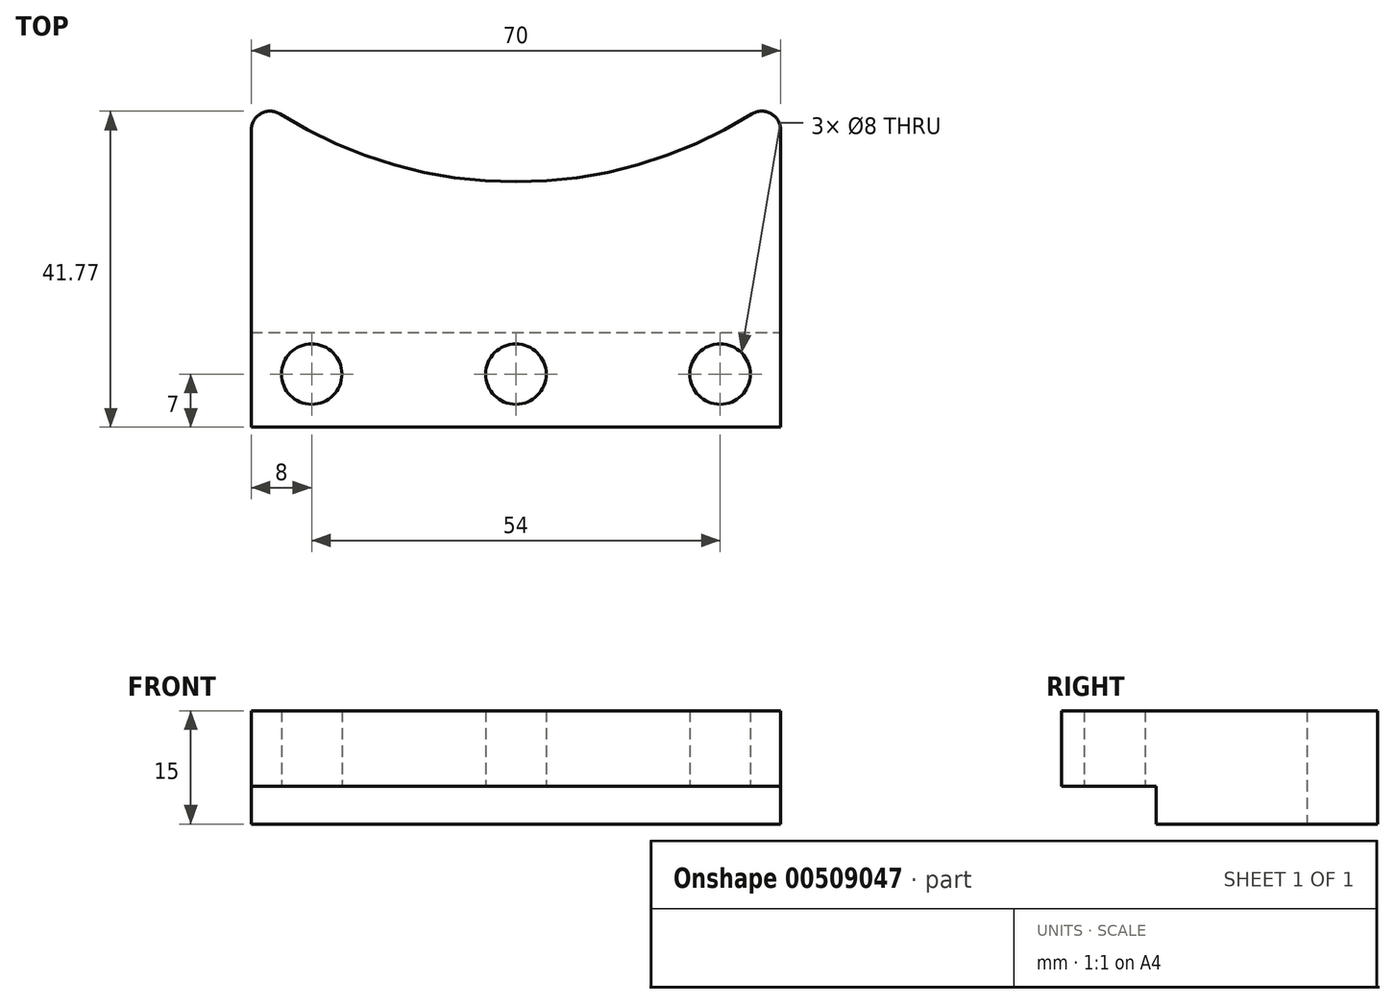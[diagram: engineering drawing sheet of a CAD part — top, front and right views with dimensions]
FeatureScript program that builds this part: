
annotation { "Feature Type Name" : "Feature", "Feature Type Description" : "" }
export const myFeature = defineFeature(function(context is Context, id is Id, definition is map)
    precondition{}
    {
        {
            var Q0;
            Q0=qCreatedBy(makeId("Top.planeOp"),FACE);
            var sketch = newSketch(context, id + "F0", { "sketchPlane" : qUnion([Q0])});
            skLineSegment(sketch, "E0.bottom", {"start": v(-35, 22) * mm, "end": v(35, 22) * mm, "construction": true});
            skLineSegment(sketch, "E0.top", {"start": v(-35, -22) * mm, "end": v(35, -22) * mm});
            skLineSegment(sketch, "E0.left", {"start": v(-35, 22) * mm, "end": v(-35, -22) * mm});
            skLineSegment(sketch, "E0.right", {"start": v(35, 22) * mm, "end": v(35, -22) * mm});
            skPoint(sketch, "E0.middle", {"position": v(0, 0) * mm});
            skLineSegment(sketch, "E1", {"start": v(0, -22) * mm, "end": v(0, 10.43) * mm, "construction": true});
            skArc(sketch, "E2", {"start": v(-35, 22) * mm, "mid": v(0, 10.43) * mm, "end": v(35, 22) * mm});
            skLineSegment(sketch, "E3", {"start": v(-35, -22) * mm, "end": v(-35, -15) * mm, "construction": true});
            skLineSegment(sketch, "E4", {"start": v(35, -15) * mm, "end": v(-35, -15) * mm, "construction": true});
            skCircle(sketch, "E5", {"center": v(0, -15) * mm, "radius": 4 * mm});
            skLineSegment(sketch, "E6", {"start": v(0, -15) * mm, "end": v(-27, -15) * mm, "construction": true});
            skLineSegment(sketch, "E7", {"start": v(0, -15) * mm, "end": v(27, -15) * mm, "construction": true});
            skCircle(sketch, "E8", {"center": v(-27, -15) * mm, "radius": 4 * mm});
            skCircle(sketch, "E9", {"center": v(27, -15) * mm, "radius": 4 * mm});
            skSolve(sketch);
        }
        {
            var Q0;
            Q0=makeQuery(id+"F0.imprint","IMPRINT",FACE,{"disambiguationData":[TD([[makeQuery(id+"F0.imprint","IMPRINT",EDGE,{"derivedFrom":sQuery(id+"F0.wireOp",EDGE,"E0.top")}),1.0]])]});
            extrude(context, id + "F1", {"entities" : qUnion([Q0]), "depth" : 40 * mm});
        }
        {
            var Q0;
            Q0=makeQuery(id+"F1.opExtrude","SWEPT_FACE",FACE,{"disambiguationData":[OSD([sQuery(id+"F0.wireOp",EDGE,"E0.right")])]});
            var sketch = newSketch(context, id + "F2", { "sketchPlane" : qUnion([Q0])});
            skLineSegment(sketch, "E10", {"start": v(-22, 0) * mm, "end": v(-9.5, 0) * mm, "construction": true});
            skLineSegment(sketch, "E11", {"start": v(-9.5, 0) * mm, "end": v(-9.5, 30) * mm});
            skLineSegment(sketch, "E12", {"start": v(-9.5, 30) * mm, "end": v(-22, 30) * mm});
            skSolve(sketch);
        }
        {
            var Q0;
            {var subQ0=sQuery(id+"F2.wireOp",EDGE,"E11");Q0=makeQuery(id+"F2.imprint","IMPRINT",FACE,{"disambiguationData":[TD([[makeQuery(id+"F2.imprint","IMPRINT",EDGE,{"derivedFrom":subQ0}),1.0]])]});}
            extrude(context, id + "F3", {"entities" : qUnion([Q0]), "operationType" : NewBodyOperationType.REMOVE, "oppositeDirection" : true, "depth" : 70 * mm});
        }
        {
            var Q0;
            Q0=makeQuery(id+"F1.opExtrude","SWEPT_EDGE",EDGE,{"disambiguationData":[OSD([sQuery(id+"F0.wireOp",EDGE,"E0.right"),sQuery(id+"F0.wireOp",EDGE,"E2")])]});
            var Q1;
            Q1=makeQuery(id+"F1.opExtrude","SWEPT_EDGE",EDGE,{"disambiguationData":[OSD([sQuery(id+"F0.wireOp",EDGE,"E0.left"),sQuery(id+"F0.wireOp",EDGE,"E2")])]});
            fillet(context, id + "F4", {"entities" : qUnion([Q0, Q1]), "radius" : 2.5 * mm, "tangentPropagation" : true, "allowEdgeOverflow" : false});
        }
        {
            var Q0;
            Q0=makeQuery(id+"F1.opExtrude","CAP_FACE",FACE,{"disambiguationData":[OSD([sQuery(id+"F0.wireOp",EDGE,"E0.top"),sQuery(id+"F0.wireOp",EDGE,"E0.left"),sQuery(id+"F0.wireOp",EDGE,"E0.right"),sQuery(id+"F0.wireOp",EDGE,"E2"),sQuery(id+"F0.wireOp",EDGE,"E5"),sQuery(id+"F0.wireOp",EDGE,"E8"),sQuery(id+"F0.wireOp",EDGE,"E9")])],"isStart":true});
            extrude(context, id + "F5", {"entities" : qUnion([Q0]), "operationType" : NewBodyOperationType.REMOVE, "oppositeDirection" : true, "depth" : 25 * mm});
        }
    });
